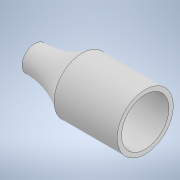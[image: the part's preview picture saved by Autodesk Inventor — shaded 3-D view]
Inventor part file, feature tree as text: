
AUTODESK INVENTOR PART (.ipt)
format: ipt  version: 2022 (Build 260153000, 153)  size: 171,008 bytes
history: native  units: mm
features: sketch x2, extrude x1, revolve x1
ambient origin geometry x8: Origin, YZ Plane, XZ Plane, XY Plane, X Axis, Y Axis, Z Axis, Center Point
bodies: Solid1 (feature_tree)
feature tree (4):
  extrude  "Extrusion1"  Depth=15.0mm
  revolve  "Revolution1"  [1 undecoded]
  sketch  "Sketch1"  dims[d0=15.0mm d1=17.75mm]
  sketch  "Sketch2"  dims[d2=20.0mm d3=0.0mm d4=15.0mm d6=4.0mm d7=1.1mm d8=90.0deg]
note: 1 required parameter value undecoded (feature->parameter linkage not recoverable at this tier; creation-order binding heuristic only, values carry confidence <= 0.55)
